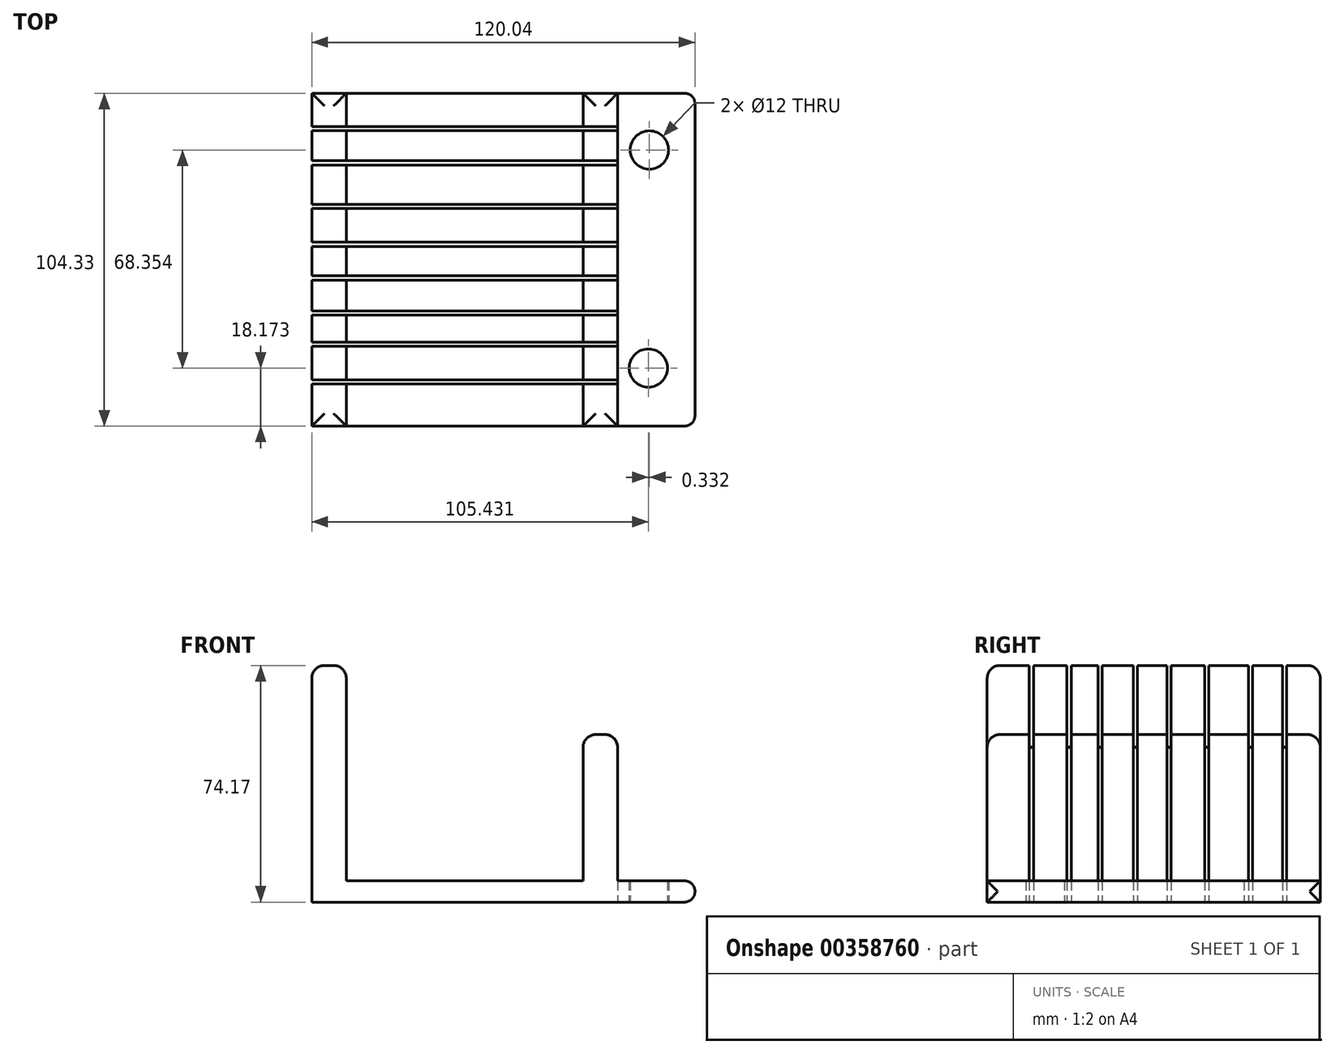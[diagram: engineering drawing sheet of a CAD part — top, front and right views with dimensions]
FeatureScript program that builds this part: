
annotation { "Feature Type Name" : "Feature", "Feature Type Description" : "" }
export const myFeature = defineFeature(function(context is Context, id is Id, definition is map)
    precondition{}
    {
        {
            var Q0;
            Q0=qCreatedBy(makeId("Front.planeOp"),FACE);
            var sketch = newSketch(context, id + "F0", { "sketchPlane" : qUnion([Q0])});
            skLineSegment(sketch, "E0", {"start": v(0, 0) * mm, "end": v(120, 0) * mm});
            skLineSegment(sketch, "E1", {"start": v(0, 0) * mm, "end": v(0, 74.17) * mm});
            skLineSegment(sketch, "E2", {"start": v(0, 74.17) * mm, "end": v(10.82, 74.17) * mm});
            skLineSegment(sketch, "E3", {"start": v(10.82, 74.17) * mm, "end": v(10.82, 6.69) * mm});
            skLineSegment(sketch, "E4", {"start": v(10.82, 6.69) * mm, "end": v(84.99, 6.69) * mm});
            skLineSegment(sketch, "E5", {"start": v(84.99, 6.69) * mm, "end": v(84.99, 52.53) * mm});
            skLineSegment(sketch, "E6", {"start": v(84.99, 52.53) * mm, "end": v(95.8, 52.53) * mm});
            skLineSegment(sketch, "E7", {"start": v(95.8, 52.53) * mm, "end": v(95.8, 6.69) * mm});
            skLineSegment(sketch, "E8", {"start": v(95.8, 6.69) * mm, "end": v(120.08, 6.69) * mm});
            skLineSegment(sketch, "E9", {"start": v(120.08, 6.69) * mm, "end": v(120, 0) * mm});
            skSolve(sketch);
        }
        {
            var Q0;
            Q0 = qSketchRegion(id + "F0", true);
            extrude(context, id + "F1", {"entities" : qUnion([Q0]), "depth" : 64.48 * 1.62 * mm});
        }
        {
            var Q0;
            Q0=makeQuery(id+"F1.opExtrude","SWEPT_FACE",FACE,{"disambiguationData":[OSD([sQuery(id+"F0.wireOp",EDGE,"E2")])]});
            var Q1;
            Q1=makeQuery(id+"F1.opExtrude","SWEPT_FACE",FACE,{"disambiguationData":[OSD([sQuery(id+"F0.wireOp",EDGE,"E6")])]});
            fillet(context, id + "F2", {"entities" : qUnion([Q0, Q1]), "radius" : 4 * mm, "tangentPropagation" : true, "allowEdgeOverflow" : false});
        }
        {
            var Q0;
            Q0=makeQuery(id+"F1.opExtrude","SWEPT_FACE",FACE,{"disambiguationData":[OSD([sQuery(id+"F0.wireOp",EDGE,"E9")])]});
            fillet(context, id + "F3", {"entities" : qUnion([Q0]), "radius" : 3.3 * mm, "allowEdgeOverflow" : false});
        }
        {
            var Q0;
            Q0=qCreatedBy(makeId("Top.planeOp"),FACE);
            var sketch = newSketch(context, id + "F4", { "sketchPlane" : qUnion([Q0])});
            skLineSegment(sketch, "E10.bottom", {"start": v(0, -10.48) * mm, "end": v(95.8, -10.48) * mm});
            skLineSegment(sketch, "E10.top", {"start": v(0, -11.78) * mm, "end": v(95.8, -11.78) * mm});
            skLineSegment(sketch, "E10.left", {"start": v(0, -10.48) * mm, "end": v(0, -11.78) * mm});
            skLineSegment(sketch, "E10.right", {"start": v(95.8, -10.48) * mm, "end": v(95.8, -11.78) * mm});
            skLineSegment(sketch, "E11.bottom", {"start": v(0, -21.18) * mm, "end": v(95.8, -21.18) * mm});
            skLineSegment(sketch, "E11.top", {"start": v(0, -22.48) * mm, "end": v(95.8, -22.48) * mm});
            skLineSegment(sketch, "E11.left", {"start": v(0, -21.18) * mm, "end": v(0, -22.48) * mm});
            skLineSegment(sketch, "E11.right", {"start": v(95.8, -21.18) * mm, "end": v(95.8, -22.48) * mm});
            skLineSegment(sketch, "E12.bottom", {"start": v(0, -34.88) * mm, "end": v(95.8, -34.88) * mm});
            skLineSegment(sketch, "E12.top", {"start": v(0, -36.18) * mm, "end": v(95.8, -36.18) * mm});
            skLineSegment(sketch, "E12.left", {"start": v(0, -34.88) * mm, "end": v(0, -36.18) * mm});
            skLineSegment(sketch, "E12.right", {"start": v(95.8, -34.88) * mm, "end": v(95.8, -36.18) * mm});
            skLineSegment(sketch, "E13.bottom", {"start": v(0, -46.73) * mm, "end": v(95.8, -46.73) * mm});
            skLineSegment(sketch, "E13.top", {"start": v(0, -48.03) * mm, "end": v(95.8, -48.03) * mm});
            skLineSegment(sketch, "E13.left", {"start": v(0, -46.73) * mm, "end": v(0, -48.03) * mm});
            skLineSegment(sketch, "E13.right", {"start": v(95.8, -46.73) * mm, "end": v(95.8, -48.03) * mm});
            skLineSegment(sketch, "E14.bottom", {"start": v(0, -57.24) * mm, "end": v(95.8, -57.24) * mm});
            skLineSegment(sketch, "E14.top", {"start": v(0, -58.54) * mm, "end": v(95.8, -58.54) * mm});
            skLineSegment(sketch, "E14.left", {"start": v(0, -57.24) * mm, "end": v(0, -58.54) * mm});
            skLineSegment(sketch, "E14.right", {"start": v(95.8, -57.24) * mm, "end": v(95.8, -58.54) * mm});
            skLineSegment(sketch, "E15.bottom", {"start": v(0, -68.28) * mm, "end": v(95.8, -68.28) * mm});
            skLineSegment(sketch, "E15.top", {"start": v(0, -69.58) * mm, "end": v(95.8, -69.58) * mm});
            skLineSegment(sketch, "E15.left", {"start": v(0, -68.28) * mm, "end": v(0, -69.58) * mm});
            skLineSegment(sketch, "E15.right", {"start": v(95.8, -68.28) * mm, "end": v(95.8, -69.58) * mm});
            skLineSegment(sketch, "E16.bottom", {"start": v(0, -78) * mm, "end": v(95.8, -78) * mm});
            skLineSegment(sketch, "E16.top", {"start": v(0, -79.3) * mm, "end": v(95.8, -79.3) * mm});
            skLineSegment(sketch, "E16.left", {"start": v(0, -78) * mm, "end": v(0, -79.3) * mm});
            skLineSegment(sketch, "E16.right", {"start": v(95.8, -78) * mm, "end": v(95.8, -79.3) * mm});
            skLineSegment(sketch, "E17.bottom", {"start": v(0, -89.83) * mm, "end": v(95.8, -89.83) * mm});
            skLineSegment(sketch, "E17.top", {"start": v(0, -91.13) * mm, "end": v(95.8, -91.13) * mm});
            skLineSegment(sketch, "E17.left", {"start": v(0, -89.83) * mm, "end": v(0, -91.13) * mm});
            skLineSegment(sketch, "E17.right", {"start": v(95.8, -89.83) * mm, "end": v(95.8, -91.13) * mm});
            skSolve(sketch);
        }
        {
            var Q0;
            Q0 = qSketchRegion(id + "F4", true);
            extrude(context, id + "F5", {"entities" : qUnion([Q0]), "operationType" : NewBodyOperationType.REMOVE, "depth" : 80 * mm});
        }
        {
            var Q0;
            Q0=qCreatedBy(makeId("Top.planeOp"),FACE);
            var sketch = newSketch(context, id + "F6", { "sketchPlane" : qUnion([Q0])});
            skCircle(sketch, "E18", {"center": v(105.76, -17.8) * mm, "radius": 6 * mm});
            skCircle(sketch, "E19", {"center": v(105.43, -86.16) * mm, "radius": 6 * mm});
            skSolve(sketch);
        }
        {
            var Q0;
            Q0=makeQuery(id+"F6.imprint","IMPRINT",FACE,{"disambiguationData":[TD([[makeQuery(id+"F6.imprint","IMPRINT",EDGE,{"derivedFrom":sQuery(id+"F6.wireOp",EDGE,"E18")}),1.0]])]});
            var Q1;
            Q1=makeQuery(id+"F6.imprint","IMPRINT",FACE,{"disambiguationData":[TD([[makeQuery(id+"F6.imprint","IMPRINT",EDGE,{"derivedFrom":sQuery(id+"F6.wireOp",EDGE,"E19")}),1.0]])]});
            var Q2;
            Q2=sQuery(id+"F6.wireOp",EDGE,"E18");
            var Q3;
            Q3=sQuery(id+"F6.wireOp",EDGE,"E19");
            extrude(context, id + "F7", {"entities" : qUnion([Q0, Q1]), "operationType" : NewBodyOperationType.REMOVE, "surfaceEntities" : qUnion([Q2, Q3]), "depth" : 25 * mm});
        }
    });
